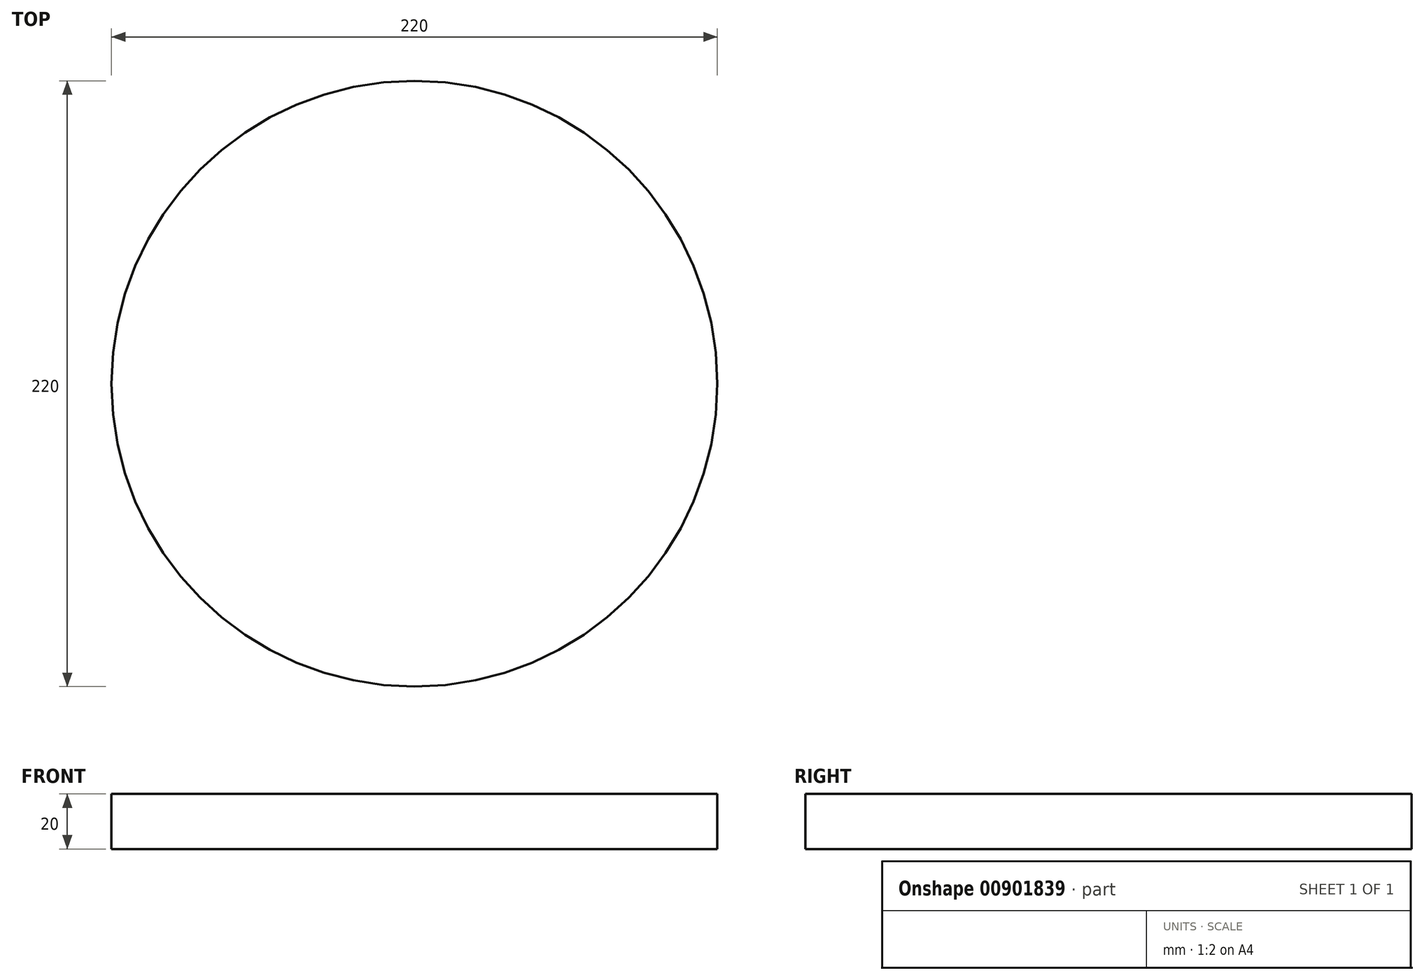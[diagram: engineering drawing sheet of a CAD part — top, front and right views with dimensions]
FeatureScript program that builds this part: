
annotation { "Feature Type Name" : "Feature", "Feature Type Description" : "" }
export const myFeature = defineFeature(function(context is Context, id is Id, definition is map)
    precondition{}
    {
        {
            var Q0;
            Q0=qCreatedBy(makeId("Top.planeOp"),FACE);
            var sketch = newSketch(context, id + "F0", { "sketchPlane" : qUnion([Q0])});
            skCircle(sketch, "E0", {"center": v(0, 0) * mm, "radius": 110 * mm});
            skSolve(sketch);
        }
        {
            var Q0;
            Q0=makeQuery(id+"F0.imprint","IMPRINT",FACE,{"disambiguationData":[TD([[makeQuery(id+"F0.imprint","IMPRINT",EDGE,{"derivedFrom":sQuery(id+"F0.wireOp",EDGE,"E0")}),1.0]])]});
            extrude(context, id + "F1", {"entities" : qUnion([Q0]), "depth" : 20 * mm, "offsetDistance" : 25 * mm});
        }
    });
